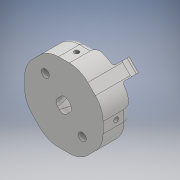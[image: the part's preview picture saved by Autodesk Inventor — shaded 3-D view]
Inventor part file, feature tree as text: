
AUTODESK INVENTOR PART (.ipt)
format: ipt  version: 2018 (Build 220112000, 112)  size: 340,480 bytes
history: native  units: mm
features: sketch x7, extrude x3, fillet x3, pattern_circular x2, hole x2, loft x1, draft x1, chamfer x1
ambient origin geometry x8: Origin, YZ Plane, XZ Plane, XY Plane, X Axis, Y Axis, Z Axis, Center Point
bodies: Body1 (feature_tree)
feature tree (20):
  extrude  "Extrusion3"  Depth=10.0mm
  loft  "Loft2"
  pattern_circular  "Circular Pattern1"  Count=4 Angle=360.0deg
  extrude  "Extrusion4"  Depth=10.0mm TaperAngle=0.0deg
  hole  "Hole1"  [1 undecoded]
  extrude  "Extrusion5"  [1 undecoded]
  draft  "FaceDraft1"
  fillet  "Fillet1"  Radius=2.0mm
  chamfer  "Chamfer1"  Distance=2.0mm Angle=45.0deg
  fillet  "Fillet2"  Radius=1.0mm
  fillet  "Fillet3"  Radius=10.0mm
  hole  "Hole2"  [1 undecoded]
  pattern_circular  "Circular Pattern2"  [2 undecoded]
  sketch  "Sketch5"  dims[d9=10.0mm d10=0.0mm d11=1.8mm]
  sketch  "Sketch6"  dims[d19=30.0mm d20=5.0mm]
  sketch  "Sketch8"  dims[d21=1.8mm]
  sketch  "Sketch9"  dims[d22=5.0mm]
  sketch  "Sketch10"  dims[d23=0.0mm d24=90.0deg]
  sketch  "Sketch11"  dims[d25=0.0mm d26=90.0deg d27=40.0mm d28=360.0deg]
  sketch  "Sketch12"  dims[d30=5.0mm d31=10.0mm d32=0.0mm d33=1.8mm d34=6.0mm d35=4.0mm d36=2.0mm d37=90.0deg d38=15.0mm d39=20.594885mm d40=10.0mm d41=0.0mm d42=-1.745329mm d43=2.0mm d44=5.0mm d45=2.0mm d46=45.0deg d47=1.0mm d48=10.0mm d49=2.0mm d50=4.0mm d51=4.0mm d52=3.0mm d53=6.0mm d54=5.0mm d55=1.0mm d56=90.0deg d57=15.0mm d58=0.0mm d59=20.0mm d60=360.0deg]
note: 5 required parameter values undecoded (feature->parameter linkage not recoverable at this tier; creation-order binding heuristic only, values carry confidence <= 0.55)
